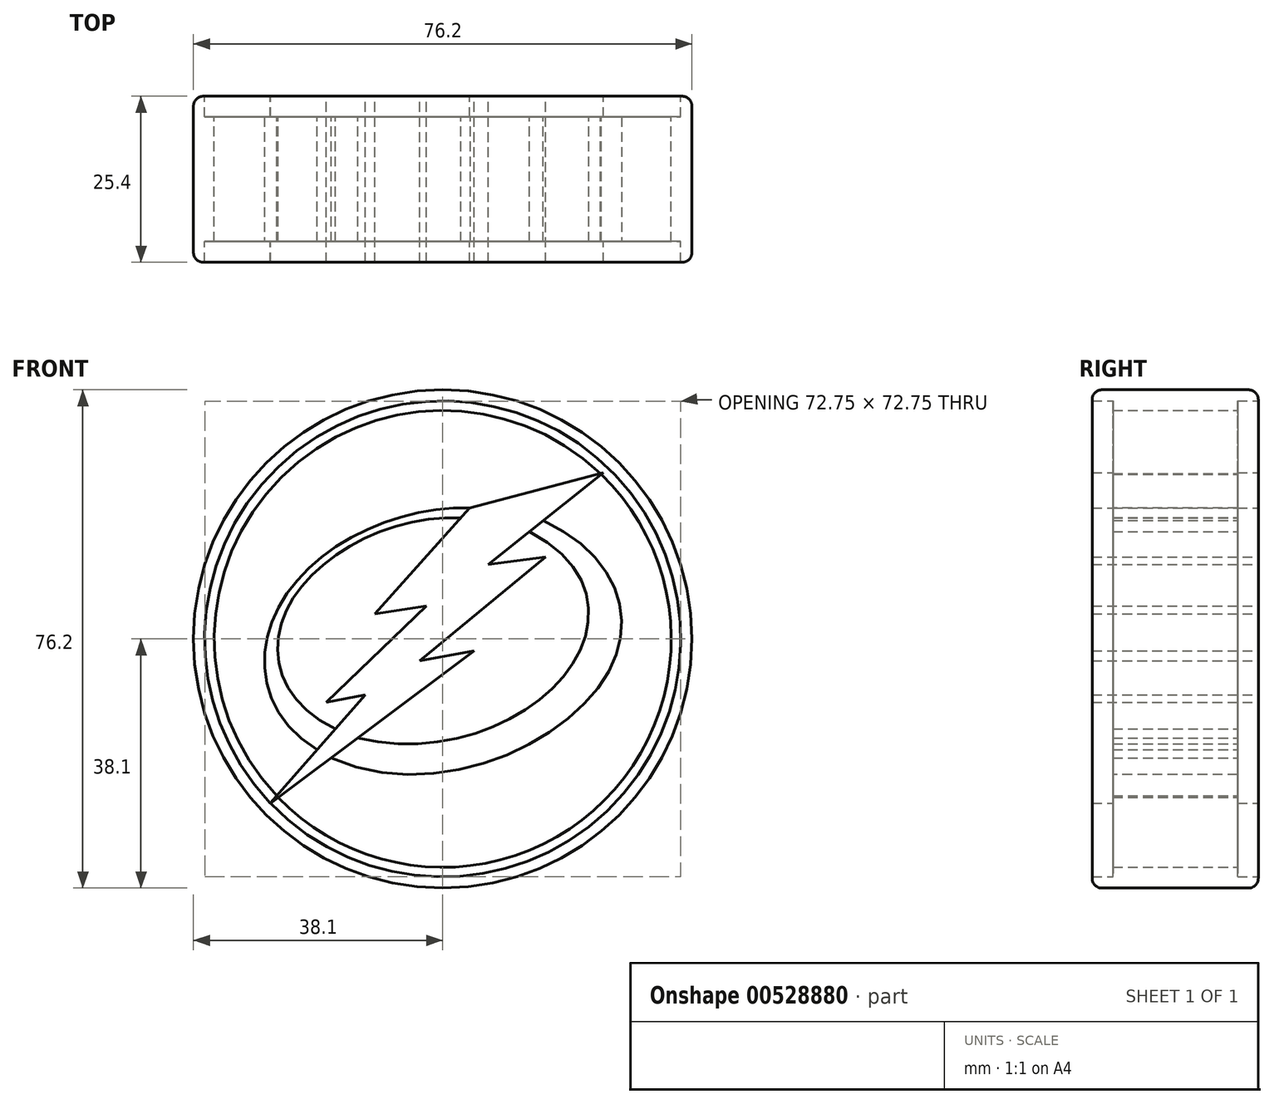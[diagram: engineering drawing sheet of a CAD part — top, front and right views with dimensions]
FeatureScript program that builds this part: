
annotation { "Feature Type Name" : "Feature", "Feature Type Description" : "" }
export const myFeature = defineFeature(function(context is Context, id is Id, definition is map)
    precondition{}
    {
        {
            var Q0;
            Q0=qCreatedBy(makeId("Front.planeOp"),FACE);
            var sketch = newSketch(context, id + "F0", { "sketchPlane" : qUnion([Q0])});
            skCircle(sketch, "E0", {"center": v(0, 0) * mm, "radius": 38.1 * mm});
            skCircle(sketch, "E1", {"center": v(0, 0) * mm, "radius": 34.93 * mm});
            skCircle(sketch, "E2", {"center": v(0, 0) * mm, "radius": 36.39 * mm});
            skSolve(sketch);
        }
        {
            var Q0;
            Q0=makeQuery(id+"F0.imprint","IMPRINT",FACE,{"disambiguationData":[TD([[makeQuery(id+"F0.imprint","IMPRINT",EDGE,{"derivedFrom":sQuery(id+"F0.wireOp",EDGE,"E0")}),1.0]])]});
            extrude(context, id + "F1", {"entities" : qUnion([Q0]), "depth" : 25.4 * mm, "offsetDistance" : 25 * mm, "symmetric" : true});
        }
        {
            var Q0;
            Q0=makeQuery(id+"F1.opExtrude","CAP_EDGE",EDGE,{"disambiguationData":[OSD([sQuery(id+"F0.wireOp",EDGE,"E0")])],"isStart":false});
            var Q1;
            Q1=makeQuery(id+"F1.opExtrude","CAP_EDGE",EDGE,{"disambiguationData":[OSD([sQuery(id+"F0.wireOp",EDGE,"E0")])],"isStart":true});
            fillet(context, id + "F2", {"entities" : qUnion([Q0, Q1]), "radius" : 1.5 * mm, "tangentPropagation" : true, "allowEdgeOverflow" : false});
        }
        {
            var Q0;
            Q0=qCreatedBy(makeId("Front.planeOp"),FACE);
            var sketch = newSketch(context, id + "F3", { "sketchPlane" : qUnion([Q0])});
            skLineSegment(sketch, "E3", {"start": v(-26.46, -25.23) * mm, "end": v(4.83, -1.85) * mm});
            skLineSegment(sketch, "E4", {"start": v(4.83, -1.85) * mm, "end": v(-3.5, -3.35) * mm});
            skLineSegment(sketch, "E5", {"start": v(-3.5, -3.35) * mm, "end": v(15.75, 12.56) * mm});
            skLineSegment(sketch, "E6", {"start": v(15.75, 12.56) * mm, "end": v(6.93, 11.42) * mm});
            skLineSegment(sketch, "E7", {"start": v(6.93, 11.42) * mm, "end": v(24.57, 25.42) * mm});
            skLineSegment(sketch, "E8", {"start": v(24.57, 25.42) * mm, "end": v(4.12, 20) * mm});
            skLineSegment(sketch, "E9", {"start": v(-26.46, -25.23) * mm, "end": v(-11.8, -8.54) * mm});
            skLineSegment(sketch, "E10", {"start": v(-11.8, -8.54) * mm, "end": v(-17.82, -9.68) * mm});
            skLineSegment(sketch, "E11", {"start": v(-17.82, -9.68) * mm, "end": v(-2.52, 5.05) * mm});
            skLineSegment(sketch, "E12", {"start": v(-2.52, 5.05) * mm, "end": v(-10.36, 3.83) * mm});
            skLineSegment(sketch, "E13", {"start": v(-10.36, 3.83) * mm, "end": v(4.12, 20) * mm});
            skSolve(sketch);
        }
        {
            var Q0;
            Q0 = qSketchRegion(id + "F3", true);
            extrude(context, id + "F4", {"entities" : qUnion([Q0]), "operationType" : NewBodyOperationType.ADD, "depth" : 25.4 * mm, "offsetDistance" : 25 * mm, "symmetric" : true});
        }
        {
            var Q0;
            Q0=makeQuery(id+"F0.imprint","IMPRINT",FACE,{"disambiguationData":[TD([[makeQuery(id+"F0.imprint","IMPRINT",EDGE,{"derivedFrom":sQuery(id+"F0.wireOp",EDGE,"E1")}),-1.0]])]});
            extrude(context, id + "F5", {"entities" : qUnion([Q0]), "operationType" : NewBodyOperationType.ADD, "depth" : 19.05 * mm, "offsetDistance" : 25 * mm, "symmetric" : true});
        }
        {
            var Q0;
            Q0=qCreatedBy(makeId("Front.planeOp"),FACE);
            var sketch = newSketch(context, id + "F6", { "sketchPlane" : qUnion([Q0])});
            skFitSpline(sketch, "E14", {"points": [v(-16.38, -13.8) * mm, v(-23.53, 5.13) * mm, v(2.83, 18.5) * mm], "startDerivative": vector(-59.57, 28.65) * mm, "endDerivative": vector(56, -3.5) * mm});
            skFitSpline(sketch, "E15", {"points": [v(-19.1, -17.02) * mm, v(-24.22, 6.32) * mm, v(4.59, 20.02) * mm], "startDerivative": vector(-61.63, 37.56) * mm, "endDerivative": vector(59.9, -2.9) * mm});
            skLineSegment(sketch, "E16", {"start": v(2.83, 18.5) * mm, "end": v(4.59, 20.02) * mm});
            skLineSegment(sketch, "E17", {"start": v(-16.38, -13.8) * mm, "end": v(-19.1, -17.02) * mm});
            skSolve(sketch);
        }
        {
            var Q0;
            Q0 = qSketchRegion(id + "F6", true);
            extrude(context, id + "F7", {"entities" : qUnion([Q0]), "operationType" : NewBodyOperationType.ADD, "depth" : 19.05 * mm, "offsetDistance" : 25 * mm, "symmetric" : true});
        }
        {
            var Q0;
            Q0=qCreatedBy(makeId("Front.planeOp"),FACE);
            var sketch = newSketch(context, id + "F8", { "sketchPlane" : qUnion([Q0])});
            skFitSpline(sketch, "E18", {"points": [v(-13.78, -14.93) * mm, v(19.58, -4.23) * mm, v(13.1, 16.5) * mm], "startDerivative": vector(70.95, -19.8) * mm, "endDerivative": vector(-71.21, 36.52) * mm});
            skFitSpline(sketch, "E19", {"points": [v(-17.47, -18.01) * mm, v(25.63, -4.47) * mm, v(14.84, 18.32) * mm], "startDerivative": vector(87.82, -40.05) * mm, "endDerivative": vector(-79, 34.8) * mm});
            skLineSegment(sketch, "E20", {"start": v(-17.47, -18.01) * mm, "end": v(-13.78, -14.93) * mm});
            skLineSegment(sketch, "E21", {"start": v(13.1, 16.5) * mm, "end": v(14.84, 18.32) * mm});
            skSolve(sketch);
        }
        {
            var Q0;
            Q0 = qSketchRegion(id + "F8", true);
            extrude(context, id + "F9", {"entities" : qUnion([Q0]), "operationType" : NewBodyOperationType.ADD, "depth" : 19.05 * mm, "offsetDistance" : 25 * mm, "symmetric" : true});
        }
    });
